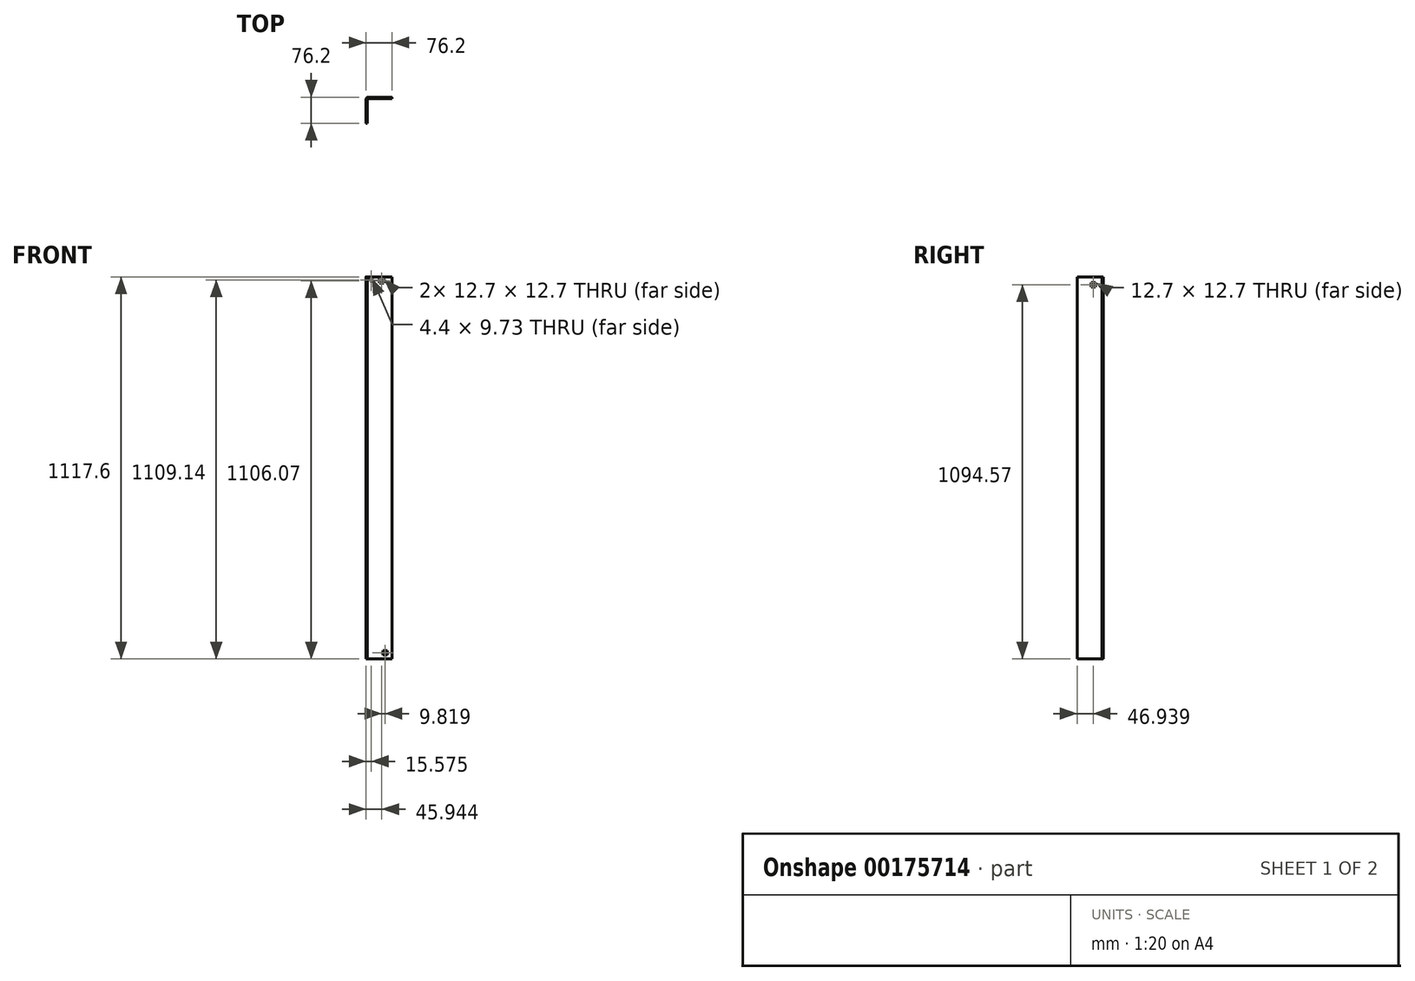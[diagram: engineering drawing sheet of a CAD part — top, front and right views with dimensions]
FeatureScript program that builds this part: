
annotation { "Feature Type Name" : "Feature", "Feature Type Description" : "" }
export const myFeature = defineFeature(function(context is Context, id is Id, definition is map)
    precondition{}
    {
        {
            var Q0;
            Q0=qCreatedBy(makeId("Top.planeOp"),FACE);
            var sketch = newSketch(context, id + "F0", { "sketchPlane" : qUnion([Q0])});
            skLineSegment(sketch, "E0.bottom", {"start": v(0, 0) * mm, "end": v(3.8, 0) * mm});
            skLineSegment(sketch, "E0.top", {"start": v(0.83, -76.2) * mm, "end": v(3.81, -76.2) * mm});
            skLineSegment(sketch, "E0.left", {"start": v(0, -6.99) * mm, "end": v(0, -75.37) * mm});
            skLineSegment(sketch, "E0.right", {"start": v(3.8, -6.99) * mm, "end": v(3.81, -76.2) * mm});
            skLineSegment(sketch, "E1.bottom", {"start": v(6.99, 0) * mm, "end": v(75.37, 0) * mm});
            skLineSegment(sketch, "E1.top", {"start": v(6.99, -3.81) * mm, "end": v(76.2, -3.81) * mm});
            skLineSegment(sketch, "E1.left", {"start": v(0, 0) * mm, "end": v(0, -3.81) * mm});
            skLineSegment(sketch, "E1.right", {"start": v(76.2, -0.83) * mm, "end": v(76.2, -3.81) * mm});
            skArc(sketch, "E2.filletArc", {"start": v(6.99, -3.8) * mm, "mid": v(4.74, -4.74) * mm, "end": v(3.81, -6.99) * mm});
            skPoint(sketch, "E3.visualSharp", {"position": v(0, 0) * mm});
            skArc(sketch, "E3.filletArc", {"start": v(6.99, 0) * mm, "mid": v(2.05, -2.05) * mm, "end": v(0, -6.99) * mm});
            skPoint(sketch, "E4.visualSharp", {"position": v(76.2, 0) * mm});
            skArc(sketch, "E4.filletArc", {"start": v(76.2, -0.83) * mm, "mid": v(75.96, -0.24) * mm, "end": v(75.37, 0) * mm});
            skPoint(sketch, "E5.visualSharp", {"position": v(0, -76.2) * mm});
            skArc(sketch, "E5.filletArc", {"start": v(0, -75.37) * mm, "mid": v(0.24, -75.96) * mm, "end": v(0.83, -76.2) * mm});
            skSolve(sketch);
        }
        {
            var Q0;
            Q0 = qSketchRegion(id + "F0", true);
            var Q1;
            Q1=makeQuery(id+"F0.imprint","IMPRINT",FACE,{"disambiguationData":[TD([[makeQuery(id+"F0.imprint","IMPRINT",EDGE,{"derivedFrom":sQuery(id+"F0.wireOp",EDGE,"E0.top")}),1.0]])]});
            extrude(context, id + "F1", {"entities" : qUnion([Q0, Q1]), "depth" : 1117.6 * mm});
        }
        {
            var Q0;
            Q0=makeQuery(id+"F1.opExtrude","SWEPT_FACE",FACE,{"disambiguationData":[OSD([sQuery(id+"F0.wireOp",EDGE,"E1.top")])]});
            extrude(context, id + "F2", {"entities" : qUnion([Q0]), "operationType" : NewBodyOperationType.REMOVE, "depth" : 12.7 * mm});
        }
        {
            var Q0;
            Q0=makeQuery(id+"F1.opExtrude","SWEPT_FACE",FACE,{"disambiguationData":[OSD([sQuery(id+"F0.wireOp",EDGE,"E1.top")])]});
            var sketch = newSketch(context, id + "F3", { "sketchPlane" : qUnion([Q0])});
            skLineSegment(sketch, "E6.bottom", {"start": v(17.78, 1104.28) * mm, "end": v(13.37, 1104.28) * mm});
            skLineSegment(sketch, "E6.top", {"start": v(17.78, 1114) * mm, "end": v(13.37, 1114) * mm});
            skLineSegment(sketch, "E6.left", {"start": v(17.78, 1104.28) * mm, "end": v(17.78, 1114) * mm});
            skLineSegment(sketch, "E6.right", {"start": v(13.37, 1104.28) * mm, "end": v(13.37, 1114) * mm});
            skPoint(sketch, "E6.middle", {"position": v(15.58, 1109.14) * mm});
            skLineSegment(sketch, "E7.bottom", {"start": v(52.3, 1099.72) * mm, "end": v(39.6, 1099.72) * mm});
            skLineSegment(sketch, "E7.top", {"start": v(52.3, 1112.42) * mm, "end": v(39.6, 1112.42) * mm});
            skLineSegment(sketch, "E7.left", {"start": v(52.3, 1099.72) * mm, "end": v(52.3, 1112.42) * mm});
            skLineSegment(sketch, "E7.right", {"start": v(39.6, 1099.72) * mm, "end": v(39.6, 1112.42) * mm});
            skPoint(sketch, "E7.middle", {"position": v(45.94, 1106.07) * mm});
            skSolve(sketch);
        }
        {
            var Q0;
            Q0=makeQuery(id+"F3.imprint","IMPRINT",FACE,{"disambiguationData":[TD([[makeQuery(id+"F3.imprint","IMPRINT",EDGE,{"derivedFrom":sQuery(id+"F3.wireOp",EDGE,"E6.bottom")}),-1.0]])]});
            var Q1;
            Q1=makeQuery(id+"F3.imprint","IMPRINT",FACE,{"disambiguationData":[TD([[makeQuery(id+"F3.imprint","IMPRINT",EDGE,{"derivedFrom":sQuery(id+"F3.wireOp",EDGE,"E7.bottom")}),-1.0]])]});
            extrude(context, id + "F4", {"entities" : qUnion([Q0, Q1]), "operationType" : NewBodyOperationType.REMOVE, "endBound" : BoundingType.THROUGH_ALL, "oppositeDirection" : true, "depth" : 25.4 * mm});
        }
        {
            var Q0;
            Q0=makeQuery(id+"F1.opExtrude","SWEPT_FACE",FACE,{"disambiguationData":[OSD([sQuery(id+"F0.wireOp",EDGE,"E0.right")])]});
            var sketch = newSketch(context, id + "F5", { "sketchPlane" : qUnion([Q0])});
            skLineSegment(sketch, "E8.bottom", {"start": v(-22.91, 1100.92) * mm, "end": v(-35.61, 1100.92) * mm});
            skLineSegment(sketch, "E8.top", {"start": v(-22.91, 1088.22) * mm, "end": v(-35.61, 1088.22) * mm});
            skLineSegment(sketch, "E8.left", {"start": v(-22.91, 1100.92) * mm, "end": v(-22.91, 1088.22) * mm});
            skLineSegment(sketch, "E8.right", {"start": v(-35.61, 1100.92) * mm, "end": v(-35.61, 1088.22) * mm});
            skSolve(sketch);
        }
        {
            var Q0;
            Q0 = qSketchRegion(id + "F5", true);
            extrude(context, id + "F6", {"entities" : qUnion([Q0]), "operationType" : NewBodyOperationType.REMOVE, "endBound" : BoundingType.THROUGH_ALL, "oppositeDirection" : true, "depth" : 25.4 * mm});
        }
        {
            var Q0;
            Q0=makeQuery(id+"F1.opExtrude","SWEPT_FACE",FACE,{"disambiguationData":[OSD([sQuery(id+"F0.wireOp",EDGE,"E1.top")])]});
            var sketch = newSketch(context, id + "F7", { "sketchPlane" : qUnion([Q0])});
            skLineSegment(sketch, "E9.bottom", {"start": v(49.41, 23.68) * mm, "end": v(62.11, 23.68) * mm});
            skLineSegment(sketch, "E9.top", {"start": v(49.41, 10.98) * mm, "end": v(62.11, 10.98) * mm});
            skLineSegment(sketch, "E9.left", {"start": v(49.41, 23.68) * mm, "end": v(49.41, 10.98) * mm});
            skLineSegment(sketch, "E9.right", {"start": v(62.11, 23.68) * mm, "end": v(62.11, 10.98) * mm});
            skSolve(sketch);
        }
        {
            var Q0;
            Q0 = qSketchRegion(id + "F7", true);
            extrude(context, id + "F8", {"entities" : qUnion([Q0]), "operationType" : NewBodyOperationType.REMOVE, "endBound" : BoundingType.THROUGH_ALL, "oppositeDirection" : true, "depth" : 25.4 * mm});
        }
    });
